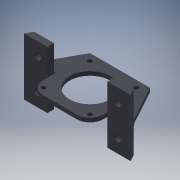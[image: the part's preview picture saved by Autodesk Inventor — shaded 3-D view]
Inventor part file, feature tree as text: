
AUTODESK INVENTOR PART (.ipt)
format: ipt  version: 2018 (Build 220112000, 112)  size: 224,768 bytes
history: native  units: mm
features: sketch x8, reference x8, extrude x7, thread x6, other x4, fillet x2, hole x1, mirror x1
ambient origin geometry x8: Origin, YZ Plane, XZ Plane, XY Plane, X Axis, Y Axis, Z Axis, Center Point
bodies: Solid1 (feature_tree)
feature tree (37):
  extrude  "Extrusion1"  Depth=90.0mm
  extrude  "Extrusion2"  Depth=6.0mm
  extrude  "Extrusion4"  Depth=40.0mm TaperAngle=0.0deg
  hole  "Hole1"  [1 undecoded]
  fillet  "Fillet1"  Radius=10.0mm
  extrude  "Extrusion5"  Depth=10.0mm
  thread  "Thread3"  [1 undecoded]
  thread  "Thread5"  [1 undecoded]
  extrude  "Extrusion6"  Depth=10.0mm
  mirror  "Mirror1"
  fillet  "Fillet2"  Radius=10.0mm
  extrude  "Extrusion8"  Depth=20.0mm
  extrude  "Extrusion9"  Depth=26.0mm
  thread  "Thread10"  [1 undecoded]
  thread  "Thread11"  [1 undecoded]
  thread  "Thread12"  [1 undecoded]
  thread  "Thread13"  [1 undecoded]
  sketch  "Sketch1"  dims[d0=90.0mm d1=90.0mm]
  sketch  "Sketch2"  dims[d2=6.0mm d3=0.0mm d10=35.0mm]
  sketch  "Sketch4"  dims[d12=10.0mm d14=40.0mm d15=46.0mm d16=0.0mm d17=0.0mm]
  sketch  "Sketch5"  dims[d22=61.0mm d23=6.0mm d24=0.0mm d25=10.0mm]
  sketch  "Sketch6"  dims[d26=10.0mm d27=10.0mm d28=10.0mm]
  sketch  "Sketch9"  dims[d30=6.0mm d31=6.0mm d32=4.0mm d33=2.0mm d34=90.0deg d35=8.0mm d36=20.594885mm d37=10.0mm]
  sketch  "Sketch11"  dims[d38=10.0mm d39=10.0mm d40=10.0mm]
  reference  "Reference1"
  reference  "Reference2"
  reference  "Reference3"
  reference  "Reference4"
  sketch  "Sketch12"  dims[d41=20.0mm d44=20.0mm d47=26.0mm d48=10.5mm d49=10.5mm d50=10.5mm d51=10.5mm d52=40.0mm d53=0.0mm d58=10.0mm d59=0.0mm d62=10.0mm d63=0.0mm d64=26.0mm d65=40.0mm d66=0.0mm d85=4.0mm d86=40.0mm d87=0.0mm d88=10.0mm d89=0.0mm d90=10.0mm d91=0.0mm d92=10.0mm d93=0.0mm d94=10.0mm d95=0.0mm d96=10.0mm d97=0.0mm]
  reference  "Reference5"
  reference  "Reference6"
  reference  "Reference7"
  reference  "Reference8"
  other  "Z axis motor mount sub-assembly.iam"
  other  "SUPPORT MAIN FRAME MOTOR-BALL SCREW-REV-B:1"
  other  "Servo Motor:1"
  other  "Body:1"
note: 7 required parameter values undecoded (feature->parameter linkage not recoverable at this tier; creation-order binding heuristic only, values carry confidence <= 0.55)
